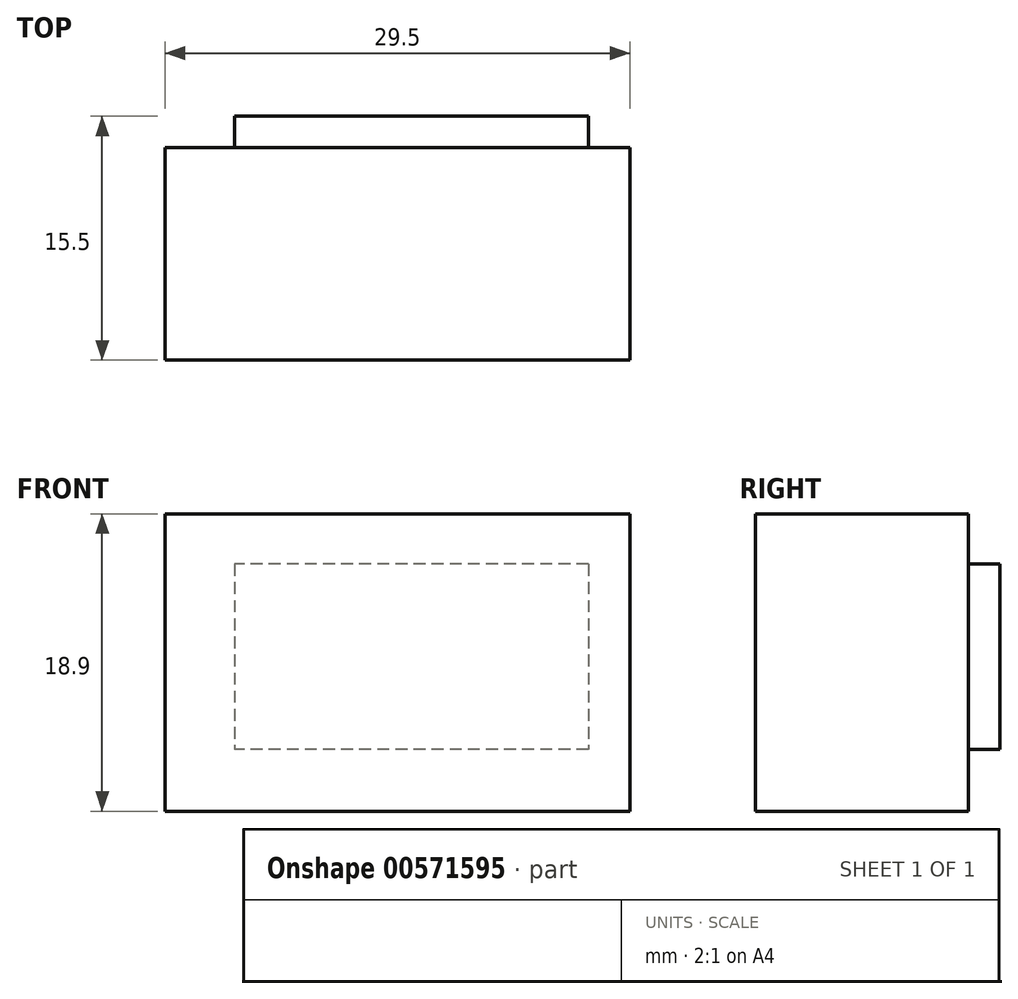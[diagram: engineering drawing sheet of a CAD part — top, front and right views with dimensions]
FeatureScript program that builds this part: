
annotation { "Feature Type Name" : "Feature", "Feature Type Description" : "" }
export const myFeature = defineFeature(function(context is Context, id is Id, definition is map)
    precondition{}
    {
        {
            var Q0;
            Q0=qCreatedBy(makeId("Front.planeOp"),FACE);
            var sketch = newSketch(context, id + "F0", { "sketchPlane" : qUnion([Q0])});
            skLineSegment(sketch, "E0.bottom", {"start": v(56.87, 3.57) * mm, "end": v(86.37, 3.57) * mm});
            skLineSegment(sketch, "E0.top", {"start": v(56.87, -15.33) * mm, "end": v(86.37, -15.33) * mm});
            skLineSegment(sketch, "E0.left", {"start": v(56.87, 3.57) * mm, "end": v(56.87, -15.33) * mm});
            skLineSegment(sketch, "E0.right", {"start": v(86.37, 3.57) * mm, "end": v(86.37, -15.33) * mm});
            skSolve(sketch);
        }
        {
            var Q0;
            Q0=makeQuery(id+"F0.imprint","IMPRINT",FACE,{"disambiguationData":[TD([[makeQuery(id+"F0.imprint","IMPRINT",EDGE,{"derivedFrom":sQuery(id+"F0.wireOp",EDGE,"E0.bottom")}),-1.0]])]});
            extrude(context, id + "F1", {"entities" : qUnion([Q0]), "depth" : 13.5 * mm, "offsetDistance" : 25 * mm});
        }
        {
            var Q0;
            Q0=makeQuery(id+"F1.opExtrude","CAP_FACE",FACE,{"disambiguationData":[OSD([sQuery(id+"F0.wireOp",EDGE,"E0.bottom"),sQuery(id+"F0.wireOp",EDGE,"E0.top"),sQuery(id+"F0.wireOp",EDGE,"E0.left"),sQuery(id+"F0.wireOp",EDGE,"E0.right")])],"isStart":true});
            var sketch = newSketch(context, id + "F2", { "sketchPlane" : qUnion([Q0])});
            skLineSegment(sketch, "E1.bottom", {"start": v(-83.74, 0.37) * mm, "end": v(-61.26, 0.37) * mm});
            skLineSegment(sketch, "E1.top", {"start": v(-83.74, -11.39) * mm, "end": v(-61.26, -11.39) * mm});
            skLineSegment(sketch, "E1.left", {"start": v(-83.74, 0.37) * mm, "end": v(-83.74, -11.39) * mm});
            skLineSegment(sketch, "E1.right", {"start": v(-61.26, 0.37) * mm, "end": v(-61.26, -11.39) * mm});
            skSolve(sketch);
        }
        {
            var Q0;
            Q0=makeQuery(id+"F2.imprint","IMPRINT",FACE,{"disambiguationData":[TD([[makeQuery(id+"F2.imprint","IMPRINT",EDGE,{"derivedFrom":sQuery(id+"F2.wireOp",EDGE,"E1.bottom")}),-1.0]])]});
            extrude(context, id + "F3", {"entities" : qUnion([Q0]), "operationType" : NewBodyOperationType.ADD, "depth" : 2 * mm, "offsetDistance" : 25 * mm});
        }
    });
